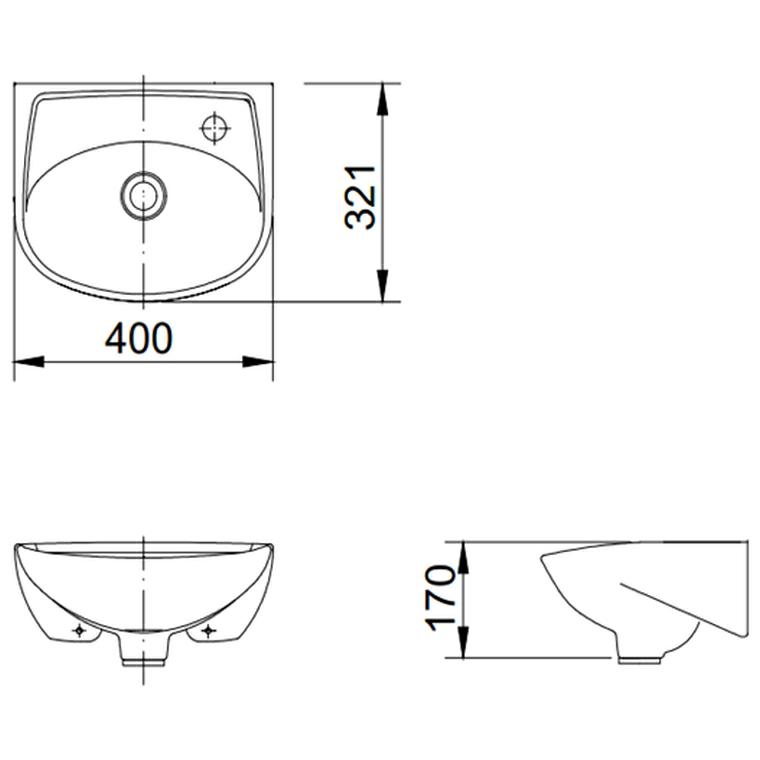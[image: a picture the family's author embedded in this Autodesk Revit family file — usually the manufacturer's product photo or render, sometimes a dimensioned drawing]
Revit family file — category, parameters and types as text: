
# Revit family: LIXIL - 709000WH - COBRA WELCOME BASIN WALL HUNG 400X321X170
name_source: partatom
category: Plumbing Fixtures
units: mm (PartAtom-declared; Revit-internal decimal feet)

## family parameters
Always vertical = Yes
Cut with Voids When Loaded = No
Enable Cutting in Views = No
Maintain Annotation Orientation = No
OmniClass Number = 23.45.00.00
OmniClass Title = Sanitary, Laundry, and Cleaning Equipment
Part Type = Normal
Room Calculation Point = No
Round Connector Dimension = Use Diameter
Shared = Yes
Work Plane-Based = No

## types (1)
- 709000WH
    CW Connection Diameter = 35 mm  [stored 0.114829 ft]
    CW Connection Radius = 18 mm
    Default Elevation = 0 mm  [stored 0 ft]
    Description = Cobra 400mm(w) x 321mm(d) x 170mm(h) Welcome wall hung basin to detail and spec. See sanware schedule. Available from Lixil.
    Hosted on lixil.co.za = https://www.lixil.co.za
    M _ BASIN = M _ LIXIL - VAAL - PORCELAIN - WHITE 01
    M _ POP UP WASTE = M _ LIXIL - STAINLESS STEEL 01
    Product Specification = Supplier: Lixil.
Product Description: Cobra Welcome Small round wall hung basin. 400mm long X 320mm wide. 1 X pre-punched tap hole on the right hand side of the basin. Wall fixing set & installation manual included. Compatible with Cobra standard-sized basin mixers.
10 Year Warranty Cobra Genuine Cobra TeamAssist
Product Code: CWLBAWH1-6DT01.
SKU Code	: 709000WH.
Barcode: 6002194040309.
Brand: Cobra.
Range: Welcome.
Category: Basins.
Sub-Category: Wall-hung.
Material: Ceramic.
Colour: White.
Package Height: 200 mm
Package Width: 420 mm
Package Length: 350 mm
Product Height: 170 mm
Product Width: 400 mm
Product Length: 321 mm
Package Volume: 29400000 mm³
Package Weight: 8 kg

Notes:
- Refer to manufacturer's and supplier's installation, maintenance and cleaning manual.
- Refer to manufacturer's and supplier's guarantees and warrantees document.
    Waste Connection Diameter = 102 mm
    Waste Connection Radius = 51 mm

note: [stored X ft] marks values corroborated as IEEE doubles in the binary element streams (Revit-internal decimal feet)

## geometry (parser evidence)
native form markers: Sweep x13
no freeform markers — native parametric forms only
